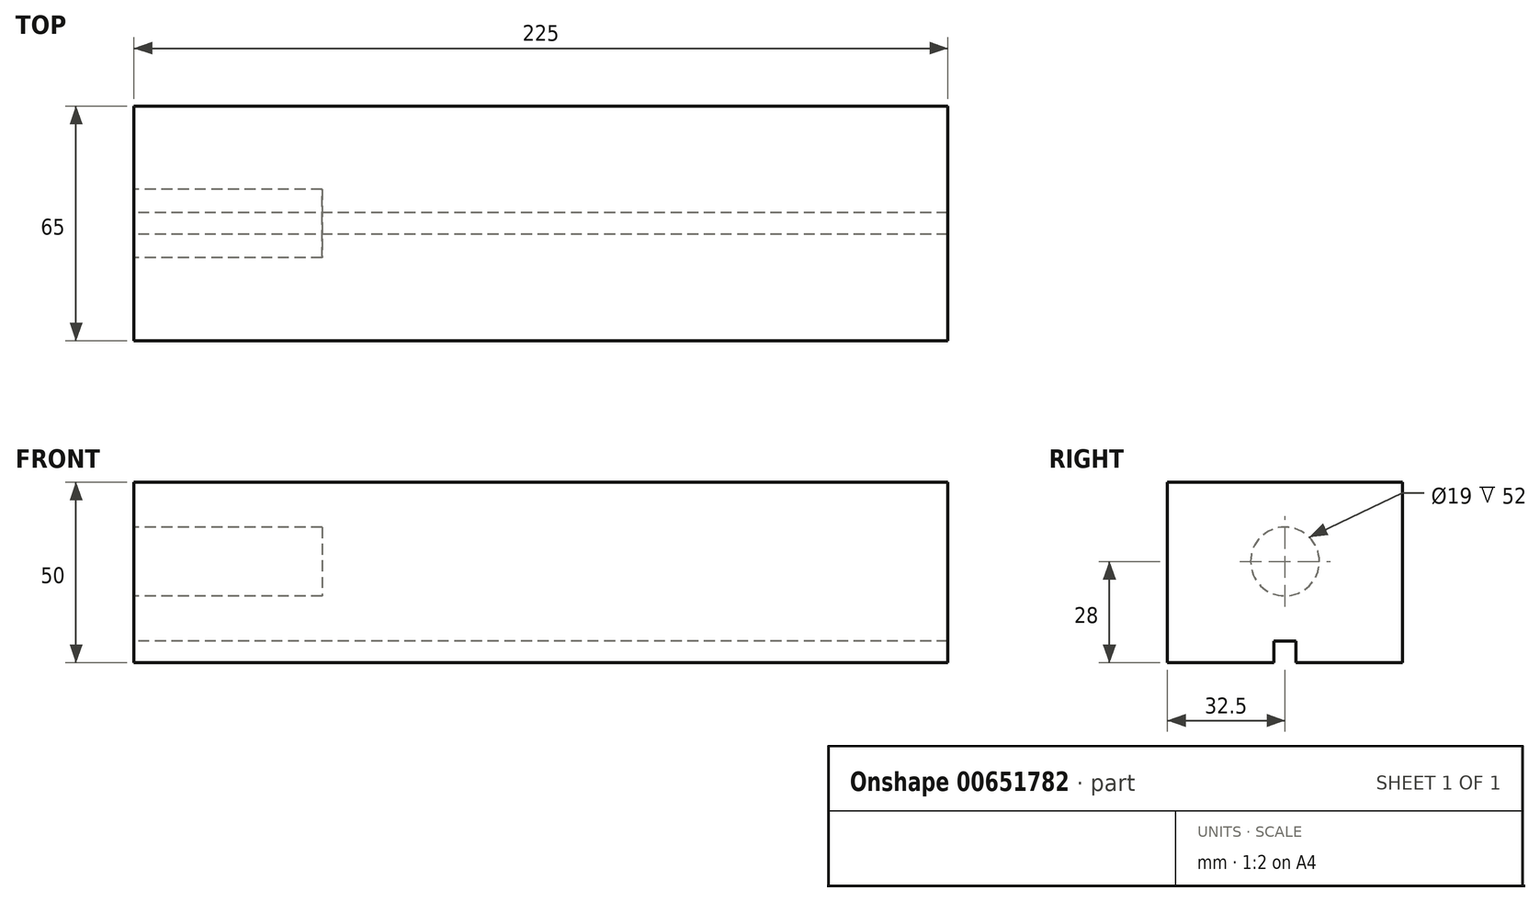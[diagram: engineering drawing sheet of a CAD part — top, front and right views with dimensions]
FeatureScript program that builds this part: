
annotation { "Feature Type Name" : "Feature", "Feature Type Description" : "" }
export const myFeature = defineFeature(function(context is Context, id is Id, definition is map)
    precondition{}
    {
        {
            var Q0;
            Q0=qCreatedBy(makeId("Right.planeOp"),FACE);
            var sketch = newSketch(context, id + "F0", { "sketchPlane" : qUnion([Q0])});
            skLineSegment(sketch, "E0", {"start": v(0, 0) * mm, "end": v(0, 50) * mm});
            skLineSegment(sketch, "E1", {"start": v(0, 50) * mm, "end": v(32.5, 50) * mm});
            skLineSegment(sketch, "E2", {"start": v(32.5, 50) * mm, "end": v(32.5, 6) * mm});
            skLineSegment(sketch, "E3", {"start": v(32.5, 6) * mm, "end": v(29.5, 6) * mm});
            skLineSegment(sketch, "E4", {"start": v(29.5, 6) * mm, "end": v(29.5, 0) * mm});
            skLineSegment(sketch, "E5", {"start": v(29.5, 0) * mm, "end": v(0, 0) * mm});
            skSolve(sketch);
        }
        {
            var Q0;
            Q0 = qSketchRegion(id + "F0", true);
            extrude(context, id + "F1", {"entities" : qUnion([Q0]), "depth" : 225 * mm, "offsetDistance" : 25 * mm});
        }
        {
            var Q0;
            Q0=makeQuery(id+"F1.opExtrude","CAP_FACE",FACE,{"disambiguationData":[OSD([sQuery(id+"F0.wireOp",EDGE,"E0"),sQuery(id+"F0.wireOp",EDGE,"E1"),sQuery(id+"F0.wireOp",EDGE,"E2"),sQuery(id+"F0.wireOp",EDGE,"E3"),sQuery(id+"F0.wireOp",EDGE,"E4"),sQuery(id+"F0.wireOp",EDGE,"E5")])],"isStart":true});
            var sketch = newSketch(context, id + "F2", { "sketchPlane" : qUnion([Q0])});
            skPoint(sketch, "E6", {"position": v(-32.5, 0) * mm});
            skPoint(sketch, "E6.positionSnap0", {"position": v(-32.5, 28) * mm});
            skCircle(sketch, "E7", {"center": v(-32.5, 28) * mm, "radius": 9.5 * mm});
            skSolve(sketch);
        }
        {
            var Q0;
            Q0 = qSketchRegion(id + "F2", true);
            extrude(context, id + "F3", {"entities" : qUnion([Q0]), "operationType" : NewBodyOperationType.REMOVE, "oppositeDirection" : true, "depth" : 52 * mm, "offsetDistance" : 25 * mm});
        }
        {
            var Q0;
            Q0=makeQuery(id+"F1.opExtrude","SWEPT_BODY",BODY,{"disambiguationData":[OSD([sQuery(id+"F0.wireOp",EDGE,"E0"),sQuery(id+"F0.wireOp",EDGE,"E1"),sQuery(id+"F0.wireOp",EDGE,"E2"),sQuery(id+"F0.wireOp",EDGE,"E3"),sQuery(id+"F0.wireOp",EDGE,"E4"),sQuery(id+"F0.wireOp",EDGE,"E5")])]});
            var Q1;
            Q1=makeQuery(id+"F1.opExtrude","SWEPT_FACE",FACE,{"disambiguationData":[OSD([sQuery(id+"F0.wireOp",EDGE,"E2")])]});
            mirror(context, id + "F4", {"operationType" : NewBodyOperationType.ADD, "entities" : qUnion([Q0]), "mirrorPlane" : qUnion([Q1])});
        }
    });
